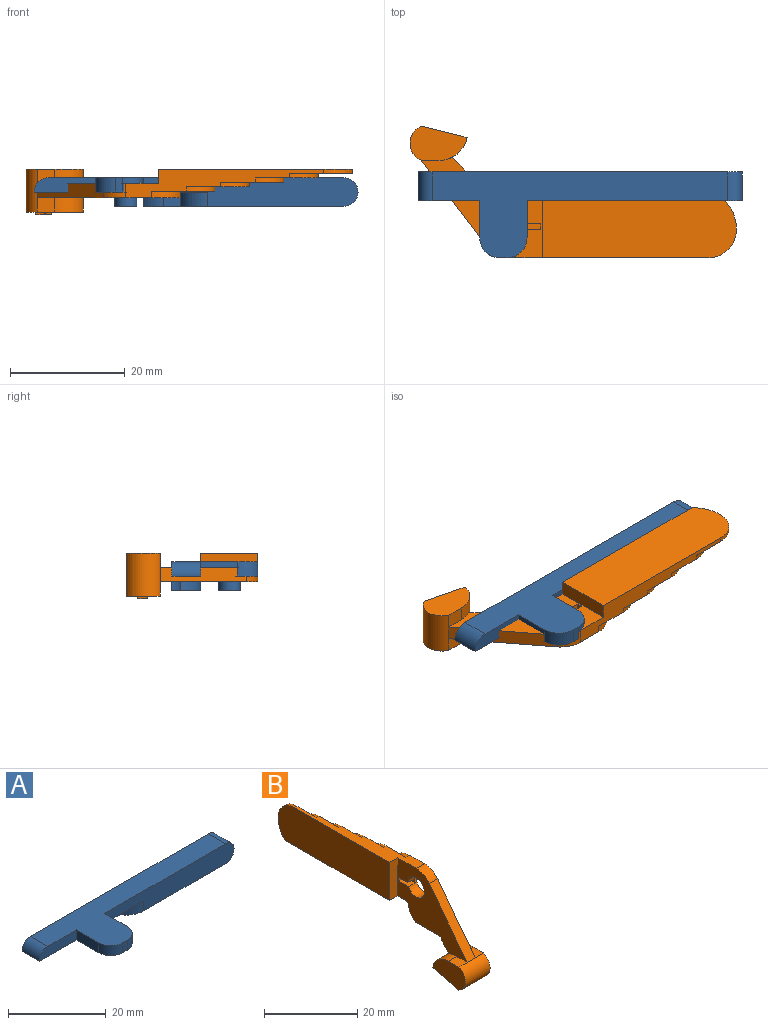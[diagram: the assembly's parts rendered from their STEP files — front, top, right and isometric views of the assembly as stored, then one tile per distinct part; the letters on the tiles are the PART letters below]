
ASSEMBLY  parts=2 mates=1
PART A: 29 faces, bbox 56.5x15x5 mm
  f0: plane 35x5mm, normal (0,0,-1), area 146.1mm2, adj f3,f5,f6,f26,f27,f28
  f1: plane 0.5x0.2mm, normal (-1,0,0), area 0.1mm2, adj f14,f20,f21,f25
  f2: plane 30.28x15mm, normal (0,0,-1), area 185.9mm2, adj f5,f6,f7,f8,f9,f10,f11,f18
  f3: cylinder r=2.5mm len=5mm, axis (0,1,0), area 39.3mm2, adj f0,f4,f5,f6
  f4: plane 51.5x15mm, normal (0,0,1), area 334.7mm2, adj f3,f5,f6,f7,f8,f9,f10,f11
  f5: plane 37.5x5mm, normal (0,-1,0), area 156.6mm2, adj f0,f2,f3,f4,f7,f28
  f6: plane 56.5x5mm, normal (0,1,0), area 231mm2, adj f0,f2,f3,f4,f8,f27
  f7: plane 6.5x2.5mm, normal (1,0,0), area 16.2mm2, adj f2,f4,f5,f22
  f8: cylinder r=2.5mm len=5mm, axis (0,1,0), area 19.6mm2, adj f2,f4,f6,f9
  f9: plane 10.75x2.5mm, normal (0,-1,0), area 25.5mm2, adj f2,f4,f8,f10
  f10: plane 6.5x2.5mm, normal (-1,0,0), area 16.2mm2, adj f2,f4,f9,f23
  f11: plane 2.5x1.25mm, normal (0,-1,0), area 3.1mm2, adj f2,f4,f22,f23
  f12: plane 2.5x0.02mm, normal (0,-1,0), area 0mm2, adj f13,f15,f16,f17
  f13: plane 2.5x0.01mm, normal (0.86,0.52,0), area 0mm2, adj f12,f15,f16,f17
  f14: cylinder r=1.9mm len=4mm, axis (0,0,1), area 42.2mm2, adj f1,f16,f18,f21,f25
  f15: plane 2.5x0.01mm, normal (-0.86,0.52,0), area 0mm2, adj f12,f13,f16,f17
  f16: plane 3.8x3.8mm, normal (0,0,-1), area 11.3mm2, adj f12,f13,f14,f15
  f17: plane 0.02x0.01mm, normal (0,0,-1), area 0mm2, adj f12,f13,f15
  f18: plane 1.76x1.5mm, normal (0,1,0), area 2.5mm2, adj f2,f14,f19,f21,f24,f25
  f19: plane 1.5x1mm, normal (1,0,0), area 1.5mm2, adj f2,f18,f20,f21
  f20: plane 2x1.5mm, normal (0,-1,0), area 2.9mm2, adj f1,f2,f19,f21,f24,f25
  f21: plane 2x1mm, normal (0,0,-1), area 1.9mm2, adj f1,f14,f18,f19,f20
  f22: cylinder r=3.5mm len=3.5mm, axis (0,0,-1), area 13.7mm2, adj f2,f4,f7,f11
  f23: cylinder r=3.5mm len=3.5mm, axis (0,0,1), area 13.7mm2, adj f2,f4,f10,f11
  f24: cylinder r=2.08mm len=4.16mm, axis (0,0,-1), area 12mm2, adj f2,f18,f20,f25
  f25: plane 4.16x4.16mm, normal (0,0,-1), area 2.1mm2, adj f1,f14,f18,f20,f24
  f26: plane 2.94x2.5mm, normal (0,-1,0), area 7.4mm2, adj f0,f2,f27,f28
  f27: cylinder r=5mm len=3.57mm, axis (0,0,-1), area 9.9mm2, adj f0,f2,f6,f26
  f28: cylinder r=5mm len=4.77mm, axis (0,0,-1), area 15.8mm2, adj f0,f2,f5,f26
PART B: 43 faces, bbox 8x57x23 mm
  f0: plane 21.1x17.57mm, normal (-1,0,0), area 170.7mm2, adj f1,f3,f7,f9,f20,f21,f22,f32
  f1: cylinder r=5mm len=4.21mm, axis (-1,0,0), area 12.5mm2, adj f0,f5,f7,f41
  f2: plane 9.96x6mm, normal (1,0,0), area 40.5mm2, adj f4,f23,f24,f33,f39
  f3: cylinder r=2.5mm len=5mm, axis (-1,0,0), area 37.2mm2, adj f0,f5,f34,f35,f37
  f4: plane 3.1x2.5mm, normal (0,0,1), area 7.8mm2, adj f2,f5,f23,f33
  f5: plane 25x17.57mm, normal (1,0,0), area 204mm2, adj f1,f3,f4,f7,f9,f19,f20,f21
  f6: plane 33.9x10mm, normal (-1,0,0), area 330.5mm2, adj f7,f8,f9,f31,f38
  f7: plane 35x5mm, normal (0,0,-1), area 86.5mm2, adj f0,f1,f5,f6,f8,f10,f11,f12
  f8: cylinder r=7.25mm len=5mm, axis (-1,0,0), area 4.2mm2, adj f6,f7,f10,f31
  f9: plane 34.53x5mm, normal (0,0,1), area 77.9mm2, adj f0,f5,f6,f10,f12,f14,f16,f18
  f10: plane 11x10mm, normal (1,0,0), area 60mm2, adj f7,f8,f9,f11,f30,f31
  f11: cylinder r=7.25mm len=5mm, axis (-1,0,0), area 4.2mm2, adj f7,f10,f12,f30
  f12: plane 11x10mm, normal (1,0,0), area 60mm2, adj f7,f9,f11,f13,f29,f30
  f13: cylinder r=7.25mm len=5mm, axis (-1,0,0), area 4.2mm2, adj f7,f12,f14,f29
  f14: plane 11x10mm, normal (1,0,0), area 60mm2, adj f7,f9,f13,f15,f28,f29
  f15: cylinder r=7.25mm len=5mm, axis (-1,0,0), area 4.2mm2, adj f7,f14,f16,f28
  f16: plane 11x10mm, normal (1,0,0), area 60mm2, adj f7,f9,f15,f17,f27,f28
  f17: cylinder r=7.25mm len=5mm, axis (-1,0,0), area 4.2mm2, adj f7,f16,f18,f27
  f18: plane 11x10mm, normal (1,0,0), area 60mm2, adj f7,f9,f17,f19,f26,f27
  f19: cylinder r=7.25mm len=5mm, axis (-1,0,0), area 6.3mm2, adj f5,f7,f18,f26
  f20: plane 15.04x11.5mm, normal (0,-0.79,0.61), area 47.3mm2, adj f0,f5,f23,f32
  f21: plane 2.5x1.34mm, normal (0,0.71,-0.71), area 4.7mm2, adj f0,f5,f33,f42
  f22: plane 3.1x2.5mm, normal (0,0,1), area 7.8mm2, adj f0,f23,f25,f33
  f23: cylinder r=3.28mm len=7.5mm, axis (-1,0,0), area 56.8mm2, adj f2,f4,f20,f22,f24,f25
  f24: plane 8x7.5mm, normal (0,0.24,-0.97), area 61.8mm2, adj f2,f23,f25,f33
  f25: plane 9.96x6mm, normal (-1,0,0), area 43.5mm2, adj f22,f23,f24,f33
  f26: cylinder r=5mm len=5mm, axis (-1,0,0), area 9mm2, adj f5,f9,f18,f19
  f27: cylinder r=5mm len=5mm, axis (-1,0,0), area 6mm2, adj f9,f16,f17,f18
  f28: cylinder r=5mm len=5mm, axis (-1,0,0), area 6mm2, adj f9,f14,f15,f16
  f29: cylinder r=5mm len=5mm, axis (-1,0,0), area 6mm2, adj f9,f12,f13,f14
  f30: cylinder r=5mm len=5mm, axis (-1,0,0), area 6mm2, adj f9,f10,f11,f12
  f31: cylinder r=5mm len=5mm, axis (-1,0,0), area 6mm2, adj f6,f8,f9,f10
  f32: cylinder r=5mm len=3.97mm, axis (-1,0,0), area 11.5mm2, adj f0,f5,f9,f20
  f33: cylinder r=5mm len=7.5mm, axis (1,0,0), area 45.3mm2, adj f0,f2,f4,f5,f21,f22,f24,f25
  f34: plane 3x2mm, normal (0,0,1), area 6mm2, adj f0,f3,f36,f37
  f35: plane 2.81x2mm, normal (0,0,-1), area 5.6mm2, adj f0,f3,f36,f37
  f36: plane 2x1mm, normal (0,-1,0), area 2mm2, adj f0,f34,f35,f37
  f37: plane 3x1mm, normal (-1,0,0), area 2.9mm2, adj f3,f34,f35,f36
  f38: plane 10x2.5mm, normal (0,-1,0), area 25mm2, adj f0,f6,f7,f9
  f39: extruded ~2.69x1.75mm, area 5.1mm2, adj f2,f40
  f40: plane 2.78x1.83mm, normal (1,0,0), area 3mm2, adj f39
  f41: plane 7.7x2.5mm, normal (0,0,-1), area 19.3mm2, adj f0,f1,f5,f42
  f42: cylinder r=5mm len=2.5mm, axis (-1,0,0), area 6mm2, adj f0,f5,f21,f41
PLACE A at identity
PLACE B rot(axis=(0.58,0.58,-0.58),120deg) t=(135.27,-5,6.5)mm
MATE revolute B.f32 <-> A.f24  axis (0,0,1) through (119.04,-10,4)mm
